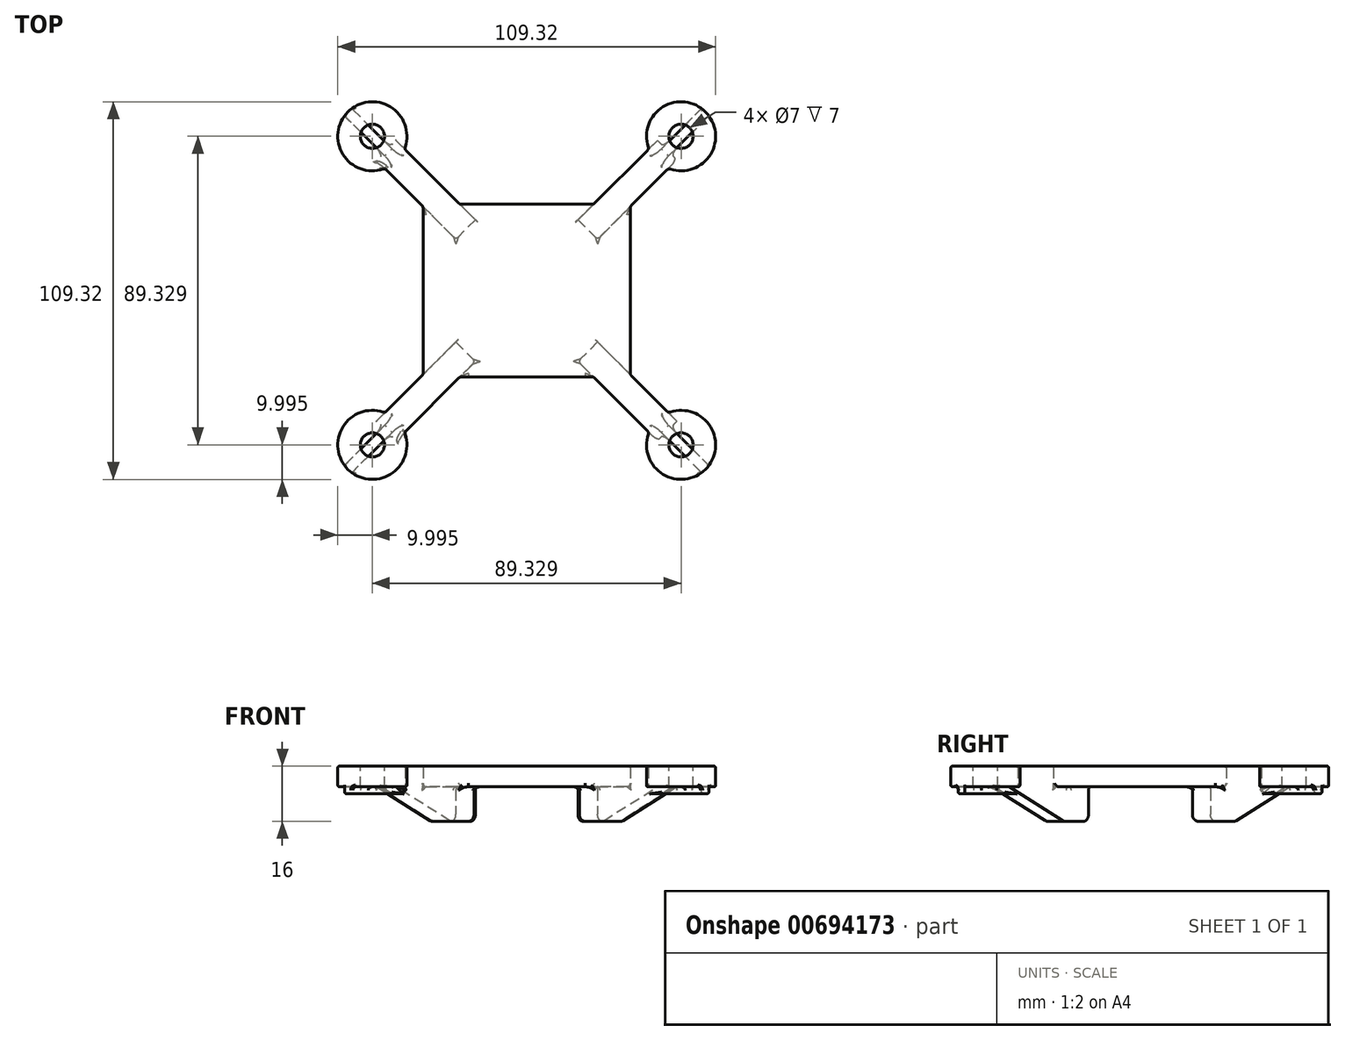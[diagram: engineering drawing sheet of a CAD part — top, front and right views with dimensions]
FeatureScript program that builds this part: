
annotation { "Feature Type Name" : "Feature", "Feature Type Description" : "" }
export const myFeature = defineFeature(function(context is Context, id is Id, definition is map)
    precondition{}
    {
        {
            var Q0;
            Q0=qCreatedBy(makeId("Top.planeOp"),FACE);
            var sketch = newSketch(context, id + "F0", { "sketchPlane" : qUnion([Q0])});
            skLineSegment(sketch, "E0.left", {"start": v(-30, 24.34) * mm, "end": v(-30, -24.34) * mm});
            skLineSegment(sketch, "E0.right", {"start": v(30, 24.34) * mm, "end": v(30, -24.34) * mm});
            skPoint(sketch, "E0.middle", {"position": v(0, 0) * mm});
            skLineSegment(sketch, "E1", {"start": v(-5.66, 0) * mm, "end": v(-30, 24.34) * mm, "construction": true});
            skLineSegment(sketch, "E2", {"start": v(-30, 24.34) * mm, "end": v(-41.01, 35.36) * mm});
            skLineSegment(sketch, "E3", {"start": v(0, 5.66) * mm, "end": v(-19.34, 25) * mm, "construction": true});
            skLineSegment(sketch, "E4", {"start": v(-19.34, 25) * mm, "end": v(-35.36, 41.01) * mm});
            skLineSegment(sketch, "E5", {"start": v(0, 5.66) * mm, "end": v(19.34, 25) * mm, "construction": true});
            skLineSegment(sketch, "E6", {"start": v(19.34, 25) * mm, "end": v(35.36, 41.01) * mm});
            skLineSegment(sketch, "E7", {"start": v(5.66, 0) * mm, "end": v(30, 24.34) * mm, "construction": true});
            skLineSegment(sketch, "E8", {"start": v(30, 24.34) * mm, "end": v(41.01, 35.36) * mm});
            skLineSegment(sketch, "E9", {"start": v(-5.66, 0) * mm, "end": v(-30, -24.34) * mm, "construction": true});
            skLineSegment(sketch, "E10", {"start": v(-30, -24.34) * mm, "end": v(-41.01, -35.36) * mm});
            skLineSegment(sketch, "E11", {"start": v(0, -5.66) * mm, "end": v(-19.34, -25) * mm, "construction": true});
            skLineSegment(sketch, "E12", {"start": v(-19.34, -25) * mm, "end": v(-35.36, -41.01) * mm});
            skLineSegment(sketch, "E13", {"start": v(0, -5.66) * mm, "end": v(19.34, -25) * mm, "construction": true});
            skLineSegment(sketch, "E14", {"start": v(19.34, -25) * mm, "end": v(35.36, -41.01) * mm});
            skLineSegment(sketch, "E15", {"start": v(5.66, 0) * mm, "end": v(30, -24.34) * mm, "construction": true});
            skLineSegment(sketch, "E16", {"start": v(30, -24.34) * mm, "end": v(41.01, -35.36) * mm});
            skLineSegment(sketch, "E17", {"start": v(0, 5.66) * mm, "end": v(0, -5.66) * mm, "construction": true});
            skLineSegment(sketch, "E18", {"start": v(-5.66, 0) * mm, "end": v(5.66, 0) * mm, "construction": true});
            skLineSegment(sketch, "E19", {"start": v(-19.34, 25) * mm, "end": v(19.34, 25) * mm});
            skLineSegment(sketch, "E20", {"start": v(-19.34, -25) * mm, "end": v(19.34, -25) * mm});
            skArc(sketch, "E21", {"start": v(-35.36, 41.01) * mm, "mid": v(-51.74, 51.74) * mm, "end": v(-41.01, 35.36) * mm});
            skArc(sketch, "E22", {"start": v(35.36, 41.01) * mm, "mid": v(51.74, 51.74) * mm, "end": v(41.01, 35.36) * mm});
            skArc(sketch, "E23", {"start": v(41.01, -35.36) * mm, "mid": v(51.74, -51.74) * mm, "end": v(35.36, -41.01) * mm});
            skArc(sketch, "E24", {"start": v(-41.01, -35.36) * mm, "mid": v(-51.74, -51.74) * mm, "end": v(-35.36, -41.01) * mm});
            skLineSegment(sketch, "E25", {"start": v(-35.36, -41.01) * mm, "end": v(-41.01, -35.36) * mm, "construction": true});
            skLineSegment(sketch, "E26", {"start": v(35.36, -41.01) * mm, "end": v(41.01, -35.36) * mm, "construction": true});
            skLineSegment(sketch, "E27", {"start": v(35.36, 41.01) * mm, "end": v(41.01, 35.36) * mm, "construction": true});
            skLineSegment(sketch, "E28", {"start": v(-35.36, 41.01) * mm, "end": v(-41.01, 35.36) * mm, "construction": true});
            skSolve(sketch);
        }
        {
            var Q0;
            Q0=qSketchRegion(id+"F0",true);
            extrude(context, id + "F1", {"entities" : qUnion([Q0]), "endBound" : BoundingType.SYMMETRIC, "depth" : 6 * mm, "offsetDistance" : 25.4 * mm});
        }
        {
            var Q0;
            Q0=makeQuery(id+"F1.opExtrude","SWEPT_FACE",FACE,{"disambiguationData":[OSD([sQuery(id+"F0.wireOp",EDGE,"E12")])]});
            cPlane(context, id + "F2", {"entities" : qUnion([Q0]), "cplaneType" : CPlaneType.OFFSET, "offset" : 0 * mm, "width" : 152.4 * mm, "height" : 152.4 * mm});
        }
        {
            var Q0;
            Q0=qCreatedBy(id+"F2.planeOp",FACE);
            var sketch = newSketch(context, id + "F3", { "sketchPlane" : qUnion([Q0])});
            skLineSegment(sketch, "E29", {"start": v(-57.5, -3) * mm, "end": v(-35, -13) * mm});
            skLineSegment(sketch, "E30", {"start": v(-35, -13) * mm, "end": v(-25, -13) * mm});
            skLineSegment(sketch, "E31", {"start": v(-25, -13) * mm, "end": v(-25, -3) * mm});
            skLineSegment(sketch, "E32", {"start": v(-25, -3) * mm, "end": v(-57.5, -3) * mm});
            skLineSegment(sketch, "E33", {"start": v(0, 36.74) * mm, "end": v(0, -57.68) * mm, "construction": true});
            skLineSegment(sketch, "E34.MirrorCS", {"start": v(25, -13) * mm, "end": v(25, -3) * mm});
            skLineSegment(sketch, "E35.MirrorCS", {"start": v(25, -3) * mm, "end": v(57.5, -3) * mm});
            skLineSegment(sketch, "E36.MirrorCS", {"start": v(57.5, -3) * mm, "end": v(35, -13) * mm});
            skLineSegment(sketch, "E37.MirrorCS", {"start": v(35, -13) * mm, "end": v(25, -13) * mm});
            skSolve(sketch);
        }
        {
            var Q0;
            Q0=qSketchRegion(id+"F3",true);
            var Q1;
            Q1=makeQuery(id+"F1.opExtrude","SWEPT_FACE",FACE,{"disambiguationData":[OSD([sQuery(id+"F0.wireOp",EDGE,"E10")])]});
            extrude(context, id + "F4", {"entities" : qUnion([Q0]), "operationType" : NewBodyOperationType.ADD, "endBound" : BoundingType.UP_TO_SURFACE, "oppositeDirection" : true, "depth" : 15 * mm, "endBoundEntityFace" : qUnion([Q1]), "offsetDistance" : 25.4 * mm});
        }
        {
            var Q0;
            Q0=makeQuery(id+"F1.opExtrude","SWEPT_FACE",FACE,{"disambiguationData":[OSD([sQuery(id+"F0.wireOp",EDGE,"E2")])]});
            cPlane(context, id + "F5", {"entities" : qUnion([Q0]), "cplaneType" : CPlaneType.OFFSET, "offset" : 0 * mm, "width" : 152.4 * mm, "height" : 152.4 * mm});
        }
        {
            var Q0;
            Q0=qCreatedBy(id+"F5.planeOp",FACE);
            var sketch = newSketch(context, id + "F6", { "sketchPlane" : qUnion([Q0])});
            skLineSegment(sketch, "E38", {"start": v(0, 30.92) * mm, "end": v(0, -51.6) * mm, "construction": true});
            skLineSegment(sketch, "E39", {"start": v(-25, -3) * mm, "end": v(-57.5, -3) * mm});
            skLineSegment(sketch, "E40", {"start": v(-57.5, -3) * mm, "end": v(-35, -13) * mm});
            skLineSegment(sketch, "E41", {"start": v(-35, -13) * mm, "end": v(-25, -13) * mm});
            skLineSegment(sketch, "E42", {"start": v(-25, -13) * mm, "end": v(-25, -3) * mm});
            skLineSegment(sketch, "E43.MirrorCS", {"start": v(25, -13) * mm, "end": v(25, -3) * mm});
            skLineSegment(sketch, "E44.MirrorCS", {"start": v(25, -3) * mm, "end": v(57.5, -3) * mm});
            skLineSegment(sketch, "E45.MirrorCS", {"start": v(57.5, -3) * mm, "end": v(35, -13) * mm});
            skLineSegment(sketch, "E46.MirrorCS", {"start": v(35, -13) * mm, "end": v(25, -13) * mm});
            skSolve(sketch);
        }
        {
            var Q0;
            Q0=qSketchRegion(id+"F6",true);
            var Q1;
            Q1=makeQuery(id+"F1.opExtrude","SWEPT_FACE",FACE,{"disambiguationData":[OSD([sQuery(id+"F0.wireOp",EDGE,"E4")])]});
            extrude(context, id + "F7", {"entities" : qUnion([Q0]), "operationType" : NewBodyOperationType.ADD, "endBound" : BoundingType.UP_TO_SURFACE, "oppositeDirection" : true, "depth" : 25.4 * mm, "endBoundEntityFace" : qUnion([Q1]), "offsetDistance" : 25.4 * mm});
        }
        {
            var Q0;
            Q0=makeQuery(id+"F1.opExtrude","CAP_FACE",FACE,{"disambiguationData":[OSD([sQuery(id+"F0.wireOp",EDGE,"E0.left"),sQuery(id+"F0.wireOp",EDGE,"E0.right"),sQuery(id+"F0.wireOp",EDGE,"E2"),sQuery(id+"F0.wireOp",EDGE,"E4"),sQuery(id+"F0.wireOp",EDGE,"E6"),sQuery(id+"F0.wireOp",EDGE,"E8"),sQuery(id+"F0.wireOp",EDGE,"E10"),sQuery(id+"F0.wireOp",EDGE,"E12"),sQuery(id+"F0.wireOp",EDGE,"E14"),sQuery(id+"F0.wireOp",EDGE,"E16"),sQuery(id+"F0.wireOp",EDGE,"U0aqChP4-xO90-fPp5-lgJY-XNEjWLDpO9Pw"),sQuery(id+"F0.wireOp",EDGE,"E19"),sQuery(id+"F0.wireOp",EDGE,"cbbJuHwt-aKsD-GqAp-nsX4-LxCeeRADLvEd"),sQuery(id+"F0.wireOp",EDGE,"bN4DHRRX-U12u-KNd2-8Xf1-whkmB7apZKRc"),sQuery(id+"F0.wireOp",EDGE,"E20"),sQuery(id+"F0.wireOp",EDGE,"p7OAdbqt-RvIZ-X6Lu-gwcG-EmbuIjXrlg1e"),sQuery(id+"F0.wireOp",EDGE,"E21"),sQuery(id+"F0.wireOp",EDGE,"E22"),sQuery(id+"F0.wireOp",EDGE,"E23"),sQuery(id+"F0.wireOp",EDGE,"E24")])],"isStart":false});
            var sketch = newSketch(context, id + "F8", { "sketchPlane" : qUnion([Q0])});
            skCircle(sketch, "E47", {"center": v(-44.66, 44.66) * mm, "radius": 3.5 * mm});
            skCircle(sketch, "E48", {"center": v(44.66, 44.66) * mm, "radius": 3.5 * mm});
            skCircle(sketch, "E49", {"center": v(44.66, -44.66) * mm, "radius": 3.5 * mm});
            skCircle(sketch, "E50", {"center": v(-44.66, -44.66) * mm, "radius": 3.5 * mm});
            skSolve(sketch);
        }
        {
            var Q0;
            Q0=qSketchRegion(id+"F8",true);
            extrude(context, id + "F9", {"entities" : qUnion([Q0]), "operationType" : NewBodyOperationType.REMOVE, "endBound" : BoundingType.THROUGH_ALL, "oppositeDirection" : true, "depth" : 25.4 * mm, "offsetDistance" : 25.4 * mm});
        }
        {
            var Q0;
            {var subQ0=sQuery(id+"F0.wireOp",EDGE,"E24");var subQ2=sQuery(id+"F0.wireOp",EDGE,"E12");var subQ3=sQuery(id+"F0.wireOp",EDGE,"E10");Q0=makeQuery(id+"F4.boolean.opBoolean","SPLIT",FACE,{"disambiguationData":[TD([makeQuery(id+"F1.opExtrude","SWEPT_FACE",FACE,{"disambiguationData":[OSD([subQ0])]})])],"derivedFrom":makeQuery(id+"F1.opExtrude","CAP_FACE",FACE,{"disambiguationData":[OSD([sQuery(id+"F0.wireOp",EDGE,"E0.left"),sQuery(id+"F0.wireOp",EDGE,"E0.right"),sQuery(id+"F0.wireOp",EDGE,"E2"),sQuery(id+"F0.wireOp",EDGE,"E4"),sQuery(id+"F0.wireOp",EDGE,"E6"),sQuery(id+"F0.wireOp",EDGE,"E8"),subQ3,subQ2,sQuery(id+"F0.wireOp",EDGE,"E14"),sQuery(id+"F0.wireOp",EDGE,"E16"),sQuery(id+"F0.wireOp",EDGE,"E19"),sQuery(id+"F0.wireOp",EDGE,"E20"),sQuery(id+"F0.wireOp",EDGE,"E21"),sQuery(id+"F0.wireOp",EDGE,"E22"),sQuery(id+"F0.wireOp",EDGE,"E23"),subQ0])],"isStart":true})});}
            var sketch = newSketch(context, id + "F10", { "sketchPlane" : qUnion([Q0])});
            skLineSegment(sketch, "E51", {"start": v(-52.72, 50.6) * mm, "end": v(-34.77, 32.64) * mm});
            skLineSegment(sketch, "E52", {"start": v(-34.77, 32.64) * mm, "end": v(-32.64, 34.77) * mm});
            skLineSegment(sketch, "E53", {"start": v(-32.64, 34.77) * mm, "end": v(-50.6, 52.72) * mm});
            skLineSegment(sketch, "E54", {"start": v(-54.84, 54.84) * mm, "end": v(59.9, -59.9) * mm, "construction": true});
            skLineSegment(sketch, "E55", {"start": v(57.6, 57.6) * mm, "end": v(-59.22, -59.22) * mm, "construction": true});
            skArc(sketch, "E56", {"start": v(-50.6, 52.72) * mm, "mid": v(-51.74, 51.74) * mm, "end": v(-52.72, 50.6) * mm});
            skLineSegment(sketch, "E57.1.0", {"start": v(-34.77, -32.64) * mm, "end": v(-52.72, -50.6) * mm});
            skArc(sketch, "E57.1.1", {"start": v(-52.72, -50.6) * mm, "mid": v(-51.74, -51.74) * mm, "end": v(-50.6, -52.72) * mm});
            skLineSegment(sketch, "E57.1.2", {"start": v(-50.6, -52.72) * mm, "end": v(-32.64, -34.77) * mm});
            skLineSegment(sketch, "E57.1.3", {"start": v(-32.64, -34.77) * mm, "end": v(-34.77, -32.64) * mm});
            skLineSegment(sketch, "E57.2.0", {"start": v(32.64, -34.77) * mm, "end": v(50.6, -52.72) * mm});
            skArc(sketch, "E57.2.1", {"start": v(50.6, -52.72) * mm, "mid": v(51.74, -51.74) * mm, "end": v(52.72, -50.6) * mm});
            skLineSegment(sketch, "E57.2.2", {"start": v(52.72, -50.6) * mm, "end": v(34.77, -32.64) * mm});
            skLineSegment(sketch, "E57.2.3", {"start": v(34.77, -32.64) * mm, "end": v(32.64, -34.77) * mm});
            skLineSegment(sketch, "E57.3.0", {"start": v(34.77, 32.64) * mm, "end": v(52.72, 50.6) * mm});
            skArc(sketch, "E57.3.1", {"start": v(52.72, 50.6) * mm, "mid": v(51.74, 51.74) * mm, "end": v(50.6, 52.72) * mm});
            skLineSegment(sketch, "E57.3.2", {"start": v(50.6, 52.72) * mm, "end": v(32.64, 34.77) * mm});
            skLineSegment(sketch, "E57.3.3", {"start": v(32.64, 34.77) * mm, "end": v(34.77, 32.64) * mm});
            skPoint(sketch, "E57.center", {"position": v(0, 0) * mm});
            skSolve(sketch);
        }
        {
            var Q0;
            Q0 = qSketchRegion(id + "F10", true);
            extrude(context, id + "F11", {"entities" : qUnion([Q0]), "operationType" : NewBodyOperationType.ADD, "depth" : 2 * mm, "offsetDistance" : 25 * mm});
        }
        {
            var Q0;
            {var subQ0=sQuery(id+"F3.wireOp",EDGE,"E32");var subQ2=sQuery(id+"F0.wireOp",EDGE,"E20");Q0=makeQuery(id+"F4.boolean.opBoolean","SPLIT",EDGE,{"disambiguationData":[TD([makeQuery(id+"F1.opExtrude","SWEPT_FACE",FACE,{"disambiguationData":[OSD([subQ2])]})])],"derivedFrom":makeQuery(id+"F4.opExtrude","CAP_EDGE",EDGE,{"disambiguationData":[OSD([subQ0])],"isStart":true})});}
            var Q1;
            Q1=makeQuery(id+"F4.opExtrude","SWEPT_EDGE",EDGE,{"disambiguationData":[OSD([sQuery(id+"F3.wireOp",EDGE,"E31"),sQuery(id+"F3.wireOp",EDGE,"E32")])]});
            var Q2;
            {var subQ0=sQuery(id+"F0.wireOp",EDGE,"E10");var subQ1=makeQuery(id+"F1.opExtrude","SWEPT_FACE",FACE,{"disambiguationData":[OSD([subQ0])]});var subQ2=sQuery(id+"F0.wireOp",EDGE,"E0.left");Q2=makeQuery(id+"F4.boolean.opBoolean","SPLIT",EDGE,{"disambiguationData":[TD([makeQuery(id+"F1.opExtrude","SWEPT_FACE",FACE,{"disambiguationData":[OSD([subQ2])]})])],"derivedFrom":makeQuery(id+"F4.opExtrude","TWEAK_EDGE",EDGE,{"derivedFrom":[subQ1,makeQuery(id+"F3.imprint","IMPRINT",EDGE,{"derivedFrom":sQuery(id+"F3.wireOp",EDGE,"E32")})]})});}
            var Q3;
            Q3=makeQuery(id+"F7.opExtrude","SWEPT_EDGE",EDGE,{"disambiguationData":[OSD([sQuery(id+"F6.wireOp",EDGE,"E43.MirrorCS"),sQuery(id+"F6.wireOp",EDGE,"E44.MirrorCS")])]});
            var Q4;
            {var subQ0=sQuery(id+"F0.wireOp",EDGE,"E0.right");var subQ1=sQuery(id+"F0.wireOp",EDGE,"E4");Q4=makeQuery(id+"F7.boolean.opBoolean","SPLIT",EDGE,{"disambiguationData":[TD([makeQuery(id+"F1.opExtrude","SWEPT_FACE",FACE,{"disambiguationData":[OSD([subQ0])]})])],"derivedFrom":makeQuery(id+"F7.opExtrude","TWEAK_EDGE",EDGE,{"derivedFrom":[makeQuery(id+"F1.opExtrude","SWEPT_FACE",FACE,{"disambiguationData":[OSD([subQ1])]}),makeQuery(id+"F6.imprint","IMPRINT",EDGE,{"derivedFrom":sQuery(id+"F6.wireOp",EDGE,"E44.MirrorCS")})]})});}
            var Q5;
            {var subQ1=sQuery(id+"F0.wireOp",EDGE,"E20");var subQ3=sQuery(id+"F6.wireOp",EDGE,"E44.MirrorCS");Q5=makeQuery(id+"F7.boolean.opBoolean","SPLIT",EDGE,{"disambiguationData":[TD([makeQuery(id+"F1.opExtrude","SWEPT_FACE",FACE,{"disambiguationData":[OSD([subQ1])]})])],"derivedFrom":makeQuery(id+"F7.opExtrude","CAP_EDGE",EDGE,{"disambiguationData":[OSD([subQ3])],"isStart":true})});}
            var Q6;
            Q6=makeQuery(id+"F1.opExtrude","SWEPT_EDGE",EDGE,{"disambiguationData":[OSD([sQuery(id+"F0.wireOp",EDGE,"E14"),sQuery(id+"F0.wireOp",EDGE,"E20")])]});
            var Q7;
            Q7=makeQuery(id+"F1.opExtrude","SWEPT_EDGE",EDGE,{"disambiguationData":[OSD([sQuery(id+"F0.wireOp",EDGE,"E12"),sQuery(id+"F0.wireOp",EDGE,"E20")])]});
            var Q8;
            Q8=makeQuery(id+"F1.opExtrude","SWEPT_EDGE",EDGE,{"disambiguationData":[OSD([sQuery(id+"F0.wireOp",EDGE,"E0.left"),sQuery(id+"F0.wireOp",EDGE,"E10")])]});
            var Q9;
            Q9=makeQuery(id+"F1.opExtrude","SWEPT_EDGE",EDGE,{"disambiguationData":[OSD([sQuery(id+"F0.wireOp",EDGE,"E0.left"),sQuery(id+"F0.wireOp",EDGE,"E2")])]});
            var Q10;
            {var subQ2=sQuery(id+"F6.wireOp",EDGE,"E39");var subQ3=sQuery(id+"F0.wireOp",EDGE,"E0.left");Q10=makeQuery(id+"F7.boolean.opBoolean","SPLIT",EDGE,{"disambiguationData":[TD([makeQuery(id+"F1.opExtrude","SWEPT_FACE",FACE,{"disambiguationData":[OSD([subQ3])]})])],"derivedFrom":makeQuery(id+"F7.opExtrude","CAP_EDGE",EDGE,{"disambiguationData":[OSD([subQ2])],"isStart":true})});}
            var Q11;
            Q11=makeQuery(id+"F7.opExtrude","SWEPT_EDGE",EDGE,{"disambiguationData":[OSD([sQuery(id+"F6.wireOp",EDGE,"E39"),sQuery(id+"F6.wireOp",EDGE,"E42")])]});
            var Q12;
            {var subQ0=sQuery(id+"F0.wireOp",EDGE,"E19");var subQ1=sQuery(id+"F0.wireOp",EDGE,"E4");var subQ2=makeQuery(id+"F1.opExtrude","SWEPT_FACE",FACE,{"disambiguationData":[OSD([subQ1])]});Q12=makeQuery(id+"F7.boolean.opBoolean","SPLIT",EDGE,{"disambiguationData":[TD([makeQuery(id+"F1.opExtrude","SWEPT_FACE",FACE,{"disambiguationData":[OSD([subQ0])]})])],"derivedFrom":makeQuery(id+"F7.opExtrude","TWEAK_EDGE",EDGE,{"derivedFrom":[subQ2,makeQuery(id+"F6.imprint","IMPRINT",EDGE,{"derivedFrom":sQuery(id+"F6.wireOp",EDGE,"E39")})]})});}
            var Q13;
            Q13=makeQuery(id+"F1.opExtrude","SWEPT_EDGE",EDGE,{"disambiguationData":[OSD([sQuery(id+"F0.wireOp",EDGE,"E4"),sQuery(id+"F0.wireOp",EDGE,"E19")])]});
            var Q14;
            Q14=makeQuery(id+"F4.opExtrude","SWEPT_EDGE",EDGE,{"disambiguationData":[OSD([sQuery(id+"F3.wireOp",EDGE,"E34.MirrorCS"),sQuery(id+"F3.wireOp",EDGE,"E35.MirrorCS")])]});
            var Q15;
            {var subQ0=sQuery(id+"F0.wireOp",EDGE,"E19");var subQ1=sQuery(id+"F0.wireOp",EDGE,"E10");Q15=makeQuery(id+"F4.boolean.opBoolean","SPLIT",EDGE,{"disambiguationData":[TD([makeQuery(id+"F1.opExtrude","SWEPT_FACE",FACE,{"disambiguationData":[OSD([subQ0])]})])],"derivedFrom":makeQuery(id+"F4.opExtrude","TWEAK_EDGE",EDGE,{"derivedFrom":[makeQuery(id+"F1.opExtrude","SWEPT_FACE",FACE,{"disambiguationData":[OSD([subQ1])]}),makeQuery(id+"F3.imprint","IMPRINT",EDGE,{"derivedFrom":sQuery(id+"F3.wireOp",EDGE,"E35.MirrorCS")})]})});}
            var Q16;
            Q16=makeQuery(id+"F1.opExtrude","SWEPT_EDGE",EDGE,{"disambiguationData":[OSD([sQuery(id+"F0.wireOp",EDGE,"E6"),sQuery(id+"F0.wireOp",EDGE,"E19")])]});
            var Q17;
            {var subQ2=sQuery(id+"F0.wireOp",EDGE,"E0.right");var subQ3=sQuery(id+"F3.wireOp",EDGE,"E35.MirrorCS");Q17=makeQuery(id+"F4.boolean.opBoolean","SPLIT",EDGE,{"disambiguationData":[TD([makeQuery(id+"F1.opExtrude","SWEPT_FACE",FACE,{"disambiguationData":[OSD([subQ2])]})])],"derivedFrom":makeQuery(id+"F4.opExtrude","CAP_EDGE",EDGE,{"disambiguationData":[OSD([subQ3])],"isStart":true})});}
            var Q18;
            Q18=makeQuery(id+"F1.opExtrude","SWEPT_EDGE",EDGE,{"disambiguationData":[OSD([sQuery(id+"F0.wireOp",EDGE,"E6"),sQuery(id+"F0.wireOp",EDGE,"E22")])]});
            var Q19;
            Q19=makeQuery(id+"F1.opExtrude","SWEPT_EDGE",EDGE,{"disambiguationData":[OSD([sQuery(id+"F0.wireOp",EDGE,"E0.right"),sQuery(id+"F0.wireOp",EDGE,"E8")])]});
            var Q20;
            Q20=makeQuery(id+"F1.opExtrude","SWEPT_EDGE",EDGE,{"disambiguationData":[OSD([sQuery(id+"F0.wireOp",EDGE,"E0.right"),sQuery(id+"F0.wireOp",EDGE,"E16")])]});
            var Q21;
            {var subQ0=sQuery(id+"F0.wireOp",EDGE,"E22");var subQ2=sQuery(id+"F0.wireOp",EDGE,"E10");Q21=makeQuery(id+"F4.boolean.opBoolean","SPLIT",EDGE,{"disambiguationData":[TD([makeQuery(id+"F1.opExtrude","SWEPT_FACE",FACE,{"disambiguationData":[OSD([subQ0])]})])],"derivedFrom":makeQuery(id+"F4.opExtrude","TWEAK_EDGE",EDGE,{"derivedFrom":[makeQuery(id+"F1.opExtrude","SWEPT_FACE",FACE,{"disambiguationData":[OSD([subQ2])]}),makeQuery(id+"F3.imprint","IMPRINT",EDGE,{"derivedFrom":sQuery(id+"F3.wireOp",EDGE,"E35.MirrorCS")})]})});}
            var Q22;
            {var subQ1=sQuery(id+"F3.wireOp",EDGE,"E36.MirrorCS");var subQ2=sQuery(id+"F0.wireOp",EDGE,"E6");Q22=makeQuery(id+"F11.boolean.opBoolean","SPLIT",EDGE,{"disambiguationData":[TD([makeQuery(id+"F1.opExtrude","SWEPT_FACE",FACE,{"disambiguationData":[OSD([subQ2])]})])],"derivedFrom":makeQuery(id+"F4.opExtrude","SWEPT_EDGE",EDGE,{"disambiguationData":[OSD([sQuery(id+"F3.wireOp",EDGE,"E35.MirrorCS"),subQ1])]})});}
            var Q23;
            Q23=makeQuery(id+"F11.boolean.opBoolean","INTERSECT",EDGE,{"derivedFrom":[makeQuery(id+"F4.opExtrude","SWEPT_FACE",FACE,{"disambiguationData":[OSD([sQuery(id+"F3.wireOp",EDGE,"E36.MirrorCS")])]}),makeQuery(id+"F11.opExtrude","SWEPT_FACE",FACE,{"disambiguationData":[OSD([sQuery(id+"F10.wireOp",EDGE,"E57.2.0")])]})]});
            var Q24;
            Q24=makeQuery(id+"F11.boolean.opBoolean","INTERSECT",EDGE,{"derivedFrom":[makeQuery(id+"F4.opExtrude","SWEPT_FACE",FACE,{"disambiguationData":[OSD([sQuery(id+"F3.wireOp",EDGE,"E36.MirrorCS")])]}),makeQuery(id+"F11.opExtrude","CAP_FACE",FACE,{"disambiguationData":[OSD([sQuery(id+"F10.wireOp",EDGE,"E57.2.0"),sQuery(id+"F10.wireOp",EDGE,"E57.2.1"),sQuery(id+"F10.wireOp",EDGE,"E57.2.2"),sQuery(id+"F10.wireOp",EDGE,"E57.2.3")])],"isStart":false})]});
            var Q25;
            Q25=makeQuery(id+"F11.boolean.opBoolean","INTERSECT",EDGE,{"derivedFrom":[makeQuery(id+"F4.opExtrude","SWEPT_FACE",FACE,{"disambiguationData":[OSD([sQuery(id+"F3.wireOp",EDGE,"E36.MirrorCS")])]}),makeQuery(id+"F11.opExtrude","SWEPT_FACE",FACE,{"disambiguationData":[OSD([sQuery(id+"F10.wireOp",EDGE,"E57.2.2")])]})]});
            var Q26;
            {var subQ0=sQuery(id+"F3.wireOp",EDGE,"E36.MirrorCS");var subQ1=sQuery(id+"F3.wireOp",EDGE,"E35.MirrorCS");var subQ2=sQuery(id+"F0.wireOp",EDGE,"E8");Q26=makeQuery(id+"F11.boolean.opBoolean","SPLIT",EDGE,{"disambiguationData":[TD([makeQuery(id+"F1.opExtrude","SWEPT_FACE",FACE,{"disambiguationData":[OSD([subQ2])]})])],"derivedFrom":makeQuery(id+"F4.opExtrude","SWEPT_EDGE",EDGE,{"disambiguationData":[OSD([subQ1,subQ0])]})});}
            var Q27;
            {var subQ1=sQuery(id+"F3.wireOp",EDGE,"E35.MirrorCS");var subQ2=sQuery(id+"F0.wireOp",EDGE,"E22");Q27=makeQuery(id+"F4.boolean.opBoolean","SPLIT",EDGE,{"disambiguationData":[TD([makeQuery(id+"F1.opExtrude","SWEPT_FACE",FACE,{"disambiguationData":[OSD([subQ2])]})])],"derivedFrom":makeQuery(id+"F4.opExtrude","CAP_EDGE",EDGE,{"disambiguationData":[OSD([subQ1])],"isStart":true})});}
            var Q28;
            Q28=makeQuery(id+"F1.opExtrude","SWEPT_EDGE",EDGE,{"disambiguationData":[OSD([sQuery(id+"F0.wireOp",EDGE,"E8"),sQuery(id+"F0.wireOp",EDGE,"E22")])]});
            var Q29;
            {var subQ0=sQuery(id+"F10.wireOp",EDGE,"E57.2.2");var subQ2=sQuery(id+"F0.wireOp",EDGE,"E22");var subQ3=makeQuery(id+"F1.opExtrude","CAP_FACE",FACE,{"disambiguationData":[OSD([sQuery(id+"F0.wireOp",EDGE,"E0.left"),sQuery(id+"F0.wireOp",EDGE,"E0.right"),sQuery(id+"F0.wireOp",EDGE,"E2"),sQuery(id+"F0.wireOp",EDGE,"E4"),sQuery(id+"F0.wireOp",EDGE,"E6"),sQuery(id+"F0.wireOp",EDGE,"E8"),sQuery(id+"F0.wireOp",EDGE,"E10"),sQuery(id+"F0.wireOp",EDGE,"E12"),sQuery(id+"F0.wireOp",EDGE,"E14"),sQuery(id+"F0.wireOp",EDGE,"E16"),sQuery(id+"F0.wireOp",EDGE,"E19"),sQuery(id+"F0.wireOp",EDGE,"E20"),sQuery(id+"F0.wireOp",EDGE,"E21"),subQ2,sQuery(id+"F0.wireOp",EDGE,"E23"),sQuery(id+"F0.wireOp",EDGE,"E24")])],"isStart":true});var subQ4=makeQuery(id+"F11.opExtrude","SWEPT_FACE",FACE,{"disambiguationData":[OSD([subQ0])]});Q29=makeQuery(id+"F11.boolean.opBoolean","SPLIT",EDGE,{"disambiguationData":[topologyDisambiguationEdgeConnected([subQ3,subQ4]),TD([makeQuery(id+"F1.opExtrude","SWEPT_FACE",FACE,{"disambiguationData":[OSD([subQ2])]})])],"derivedFrom":makeQuery(id+"F11.opExtrude","CAP_EDGE",EDGE,{"disambiguationData":[OSD([subQ0])],"isStart":true})});}
            var Q30;
            {var subQ0=sQuery(id+"F10.wireOp",EDGE,"E57.2.0");var subQ1=makeQuery(id+"F11.opExtrude","SWEPT_FACE",FACE,{"disambiguationData":[OSD([subQ0])]});var subQ2=sQuery(id+"F0.wireOp",EDGE,"E22");var subQ4=makeQuery(id+"F1.opExtrude","CAP_FACE",FACE,{"disambiguationData":[OSD([sQuery(id+"F0.wireOp",EDGE,"E0.left"),sQuery(id+"F0.wireOp",EDGE,"E0.right"),sQuery(id+"F0.wireOp",EDGE,"E2"),sQuery(id+"F0.wireOp",EDGE,"E4"),sQuery(id+"F0.wireOp",EDGE,"E6"),sQuery(id+"F0.wireOp",EDGE,"E8"),sQuery(id+"F0.wireOp",EDGE,"E10"),sQuery(id+"F0.wireOp",EDGE,"E12"),sQuery(id+"F0.wireOp",EDGE,"E14"),sQuery(id+"F0.wireOp",EDGE,"E16"),sQuery(id+"F0.wireOp",EDGE,"E19"),sQuery(id+"F0.wireOp",EDGE,"E20"),sQuery(id+"F0.wireOp",EDGE,"E21"),subQ2,sQuery(id+"F0.wireOp",EDGE,"E23"),sQuery(id+"F0.wireOp",EDGE,"E24")])],"isStart":true});Q30=makeQuery(id+"F11.boolean.opBoolean","SPLIT",EDGE,{"disambiguationData":[topologyDisambiguationEdgeConnected([subQ4,subQ1]),TD([makeQuery(id+"F1.opExtrude","SWEPT_FACE",FACE,{"disambiguationData":[OSD([subQ2])]})])],"derivedFrom":makeQuery(id+"F11.opExtrude","CAP_EDGE",EDGE,{"disambiguationData":[OSD([subQ0])],"isStart":true})});}
            var Q31;
            Q31=makeQuery(id+"F1.opExtrude","SWEPT_EDGE",EDGE,{"disambiguationData":[OSD([sQuery(id+"F0.wireOp",EDGE,"E2"),sQuery(id+"F0.wireOp",EDGE,"E21")])]});
            var Q32;
            {var subQ1=sQuery(id+"F6.wireOp",EDGE,"E39");var subQ3=sQuery(id+"F0.wireOp",EDGE,"E21");Q32=makeQuery(id+"F7.boolean.opBoolean","SPLIT",EDGE,{"disambiguationData":[TD([makeQuery(id+"F1.opExtrude","SWEPT_FACE",FACE,{"disambiguationData":[OSD([subQ3])]})])],"derivedFrom":makeQuery(id+"F7.opExtrude","CAP_EDGE",EDGE,{"disambiguationData":[OSD([subQ1])],"isStart":true})});}
            var Q33;
            {var subQ0=sQuery(id+"F6.wireOp",EDGE,"E40");var subQ1=sQuery(id+"F6.wireOp",EDGE,"E39");var subQ2=sQuery(id+"F0.wireOp",EDGE,"E2");Q33=makeQuery(id+"F11.boolean.opBoolean","SPLIT",EDGE,{"disambiguationData":[TD([makeQuery(id+"F1.opExtrude","SWEPT_FACE",FACE,{"disambiguationData":[OSD([subQ2])]})])],"derivedFrom":makeQuery(id+"F7.opExtrude","SWEPT_EDGE",EDGE,{"disambiguationData":[OSD([subQ1,subQ0])]})});}
            var Q34;
            Q34=makeQuery(id+"F11.boolean.opBoolean","INTERSECT",EDGE,{"derivedFrom":[makeQuery(id+"F7.opExtrude","SWEPT_FACE",FACE,{"disambiguationData":[OSD([sQuery(id+"F6.wireOp",EDGE,"E40")])]}),makeQuery(id+"F11.opExtrude","SWEPT_FACE",FACE,{"disambiguationData":[OSD([sQuery(id+"F10.wireOp",EDGE,"E57.1.0")])]})]});
            var Q35;
            Q35=makeQuery(id+"F11.boolean.opBoolean","INTERSECT",EDGE,{"derivedFrom":[makeQuery(id+"F7.opExtrude","SWEPT_FACE",FACE,{"disambiguationData":[OSD([sQuery(id+"F6.wireOp",EDGE,"E40")])]}),makeQuery(id+"F11.opExtrude","CAP_FACE",FACE,{"disambiguationData":[OSD([sQuery(id+"F10.wireOp",EDGE,"E57.1.0"),sQuery(id+"F10.wireOp",EDGE,"E57.1.1"),sQuery(id+"F10.wireOp",EDGE,"E57.1.2"),sQuery(id+"F10.wireOp",EDGE,"E57.1.3")])],"isStart":false})]});
            var Q36;
            Q36=makeQuery(id+"F11.boolean.opBoolean","INTERSECT",EDGE,{"derivedFrom":[makeQuery(id+"F7.opExtrude","SWEPT_FACE",FACE,{"disambiguationData":[OSD([sQuery(id+"F6.wireOp",EDGE,"E40")])]}),makeQuery(id+"F11.opExtrude","SWEPT_FACE",FACE,{"disambiguationData":[OSD([sQuery(id+"F10.wireOp",EDGE,"E57.1.2")])]})]});
            var Q37;
            {var subQ0=sQuery(id+"F0.wireOp",EDGE,"E4");var subQ1=sQuery(id+"F6.wireOp",EDGE,"E40");Q37=makeQuery(id+"F11.boolean.opBoolean","SPLIT",EDGE,{"disambiguationData":[TD([makeQuery(id+"F1.opExtrude","SWEPT_FACE",FACE,{"disambiguationData":[OSD([subQ0])]})])],"derivedFrom":makeQuery(id+"F7.opExtrude","SWEPT_EDGE",EDGE,{"disambiguationData":[OSD([sQuery(id+"F6.wireOp",EDGE,"E39"),subQ1])]})});}
            var Q38;
            {var subQ0=sQuery(id+"F0.wireOp",EDGE,"E21");var subQ1=sQuery(id+"F0.wireOp",EDGE,"E4");var subQ2=makeQuery(id+"F1.opExtrude","SWEPT_FACE",FACE,{"disambiguationData":[OSD([subQ1])]});Q38=makeQuery(id+"F7.boolean.opBoolean","SPLIT",EDGE,{"disambiguationData":[TD([makeQuery(id+"F1.opExtrude","SWEPT_FACE",FACE,{"disambiguationData":[OSD([subQ0])]})])],"derivedFrom":makeQuery(id+"F7.opExtrude","TWEAK_EDGE",EDGE,{"derivedFrom":[subQ2,makeQuery(id+"F6.imprint","IMPRINT",EDGE,{"derivedFrom":sQuery(id+"F6.wireOp",EDGE,"E39")})]})});}
            var Q39;
            Q39=makeQuery(id+"F1.opExtrude","SWEPT_EDGE",EDGE,{"disambiguationData":[OSD([sQuery(id+"F0.wireOp",EDGE,"E4"),sQuery(id+"F0.wireOp",EDGE,"E21")])]});
            var Q40;
            {var subQ0=sQuery(id+"F10.wireOp",EDGE,"E57.1.2");var subQ2=sQuery(id+"F0.wireOp",EDGE,"E21");var subQ3=makeQuery(id+"F1.opExtrude","CAP_FACE",FACE,{"disambiguationData":[OSD([sQuery(id+"F0.wireOp",EDGE,"E0.left"),sQuery(id+"F0.wireOp",EDGE,"E0.right"),sQuery(id+"F0.wireOp",EDGE,"E2"),sQuery(id+"F0.wireOp",EDGE,"E4"),sQuery(id+"F0.wireOp",EDGE,"E6"),sQuery(id+"F0.wireOp",EDGE,"E8"),sQuery(id+"F0.wireOp",EDGE,"E10"),sQuery(id+"F0.wireOp",EDGE,"E12"),sQuery(id+"F0.wireOp",EDGE,"E14"),sQuery(id+"F0.wireOp",EDGE,"E16"),sQuery(id+"F0.wireOp",EDGE,"E19"),sQuery(id+"F0.wireOp",EDGE,"E20"),subQ2,sQuery(id+"F0.wireOp",EDGE,"E22"),sQuery(id+"F0.wireOp",EDGE,"E23"),sQuery(id+"F0.wireOp",EDGE,"E24")])],"isStart":true});var subQ4=makeQuery(id+"F11.opExtrude","SWEPT_FACE",FACE,{"disambiguationData":[OSD([subQ0])]});Q40=makeQuery(id+"F11.boolean.opBoolean","SPLIT",EDGE,{"disambiguationData":[topologyDisambiguationEdgeConnected([subQ3,subQ4]),TD([makeQuery(id+"F1.opExtrude","SWEPT_FACE",FACE,{"disambiguationData":[OSD([subQ2])]})])],"derivedFrom":makeQuery(id+"F11.opExtrude","CAP_EDGE",EDGE,{"disambiguationData":[OSD([subQ0])],"isStart":true})});}
            var Q41;
            {var subQ0=sQuery(id+"F10.wireOp",EDGE,"E57.1.0");var subQ1=makeQuery(id+"F11.opExtrude","SWEPT_FACE",FACE,{"disambiguationData":[OSD([subQ0])]});var subQ2=sQuery(id+"F0.wireOp",EDGE,"E21");var subQ3=makeQuery(id+"F1.opExtrude","CAP_FACE",FACE,{"disambiguationData":[OSD([sQuery(id+"F0.wireOp",EDGE,"E0.left"),sQuery(id+"F0.wireOp",EDGE,"E0.right"),sQuery(id+"F0.wireOp",EDGE,"E2"),sQuery(id+"F0.wireOp",EDGE,"E4"),sQuery(id+"F0.wireOp",EDGE,"E6"),sQuery(id+"F0.wireOp",EDGE,"E8"),sQuery(id+"F0.wireOp",EDGE,"E10"),sQuery(id+"F0.wireOp",EDGE,"E12"),sQuery(id+"F0.wireOp",EDGE,"E14"),sQuery(id+"F0.wireOp",EDGE,"E16"),sQuery(id+"F0.wireOp",EDGE,"E19"),sQuery(id+"F0.wireOp",EDGE,"E20"),subQ2,sQuery(id+"F0.wireOp",EDGE,"E22"),sQuery(id+"F0.wireOp",EDGE,"E23"),sQuery(id+"F0.wireOp",EDGE,"E24")])],"isStart":true});Q41=makeQuery(id+"F11.boolean.opBoolean","SPLIT",EDGE,{"disambiguationData":[topologyDisambiguationEdgeConnected([subQ3,subQ1]),TD([makeQuery(id+"F1.opExtrude","SWEPT_FACE",FACE,{"disambiguationData":[OSD([subQ2])]})])],"derivedFrom":makeQuery(id+"F11.opExtrude","CAP_EDGE",EDGE,{"disambiguationData":[OSD([subQ0])],"isStart":true})});}
            var Q42;
            Q42=makeQuery(id+"F1.opExtrude","SWEPT_EDGE",EDGE,{"disambiguationData":[OSD([sQuery(id+"F0.wireOp",EDGE,"E12"),sQuery(id+"F0.wireOp",EDGE,"E24")])]});
            var Q43;
            {var subQ0=sQuery(id+"F0.wireOp",EDGE,"E24");var subQ1=sQuery(id+"F3.wireOp",EDGE,"E32");Q43=makeQuery(id+"F4.boolean.opBoolean","SPLIT",EDGE,{"disambiguationData":[TD([makeQuery(id+"F1.opExtrude","SWEPT_FACE",FACE,{"disambiguationData":[OSD([subQ0])]})])],"derivedFrom":makeQuery(id+"F4.opExtrude","CAP_EDGE",EDGE,{"disambiguationData":[OSD([subQ1])],"isStart":true})});}
            var Q44;
            {var subQ0=sQuery(id+"F3.wireOp",EDGE,"E32");var subQ1=sQuery(id+"F3.wireOp",EDGE,"E29");var subQ2=sQuery(id+"F0.wireOp",EDGE,"E12");Q44=makeQuery(id+"F11.boolean.opBoolean","SPLIT",EDGE,{"disambiguationData":[TD([makeQuery(id+"F1.opExtrude","SWEPT_FACE",FACE,{"disambiguationData":[OSD([subQ2])]})])],"derivedFrom":makeQuery(id+"F4.opExtrude","SWEPT_EDGE",EDGE,{"disambiguationData":[OSD([subQ1,subQ0])]})});}
            var Q45;
            Q45=makeQuery(id+"F11.boolean.opBoolean","INTERSECT",EDGE,{"derivedFrom":[makeQuery(id+"F4.opExtrude","SWEPT_FACE",FACE,{"disambiguationData":[OSD([sQuery(id+"F3.wireOp",EDGE,"E29")])]}),makeQuery(id+"F11.opExtrude","SWEPT_FACE",FACE,{"disambiguationData":[OSD([sQuery(id+"F10.wireOp",EDGE,"E53")])]})]});
            var Q46;
            Q46=makeQuery(id+"F11.boolean.opBoolean","INTERSECT",EDGE,{"derivedFrom":[makeQuery(id+"F4.opExtrude","SWEPT_FACE",FACE,{"disambiguationData":[OSD([sQuery(id+"F3.wireOp",EDGE,"E29")])]}),makeQuery(id+"F11.opExtrude","CAP_FACE",FACE,{"disambiguationData":[OSD([sQuery(id+"F10.wireOp",EDGE,"E51"),sQuery(id+"F10.wireOp",EDGE,"E52"),sQuery(id+"F10.wireOp",EDGE,"E53"),sQuery(id+"F10.wireOp",EDGE,"E56")])],"isStart":false})]});
            var Q47;
            Q47=makeQuery(id+"F11.boolean.opBoolean","INTERSECT",EDGE,{"derivedFrom":[makeQuery(id+"F4.opExtrude","SWEPT_FACE",FACE,{"disambiguationData":[OSD([sQuery(id+"F3.wireOp",EDGE,"E29")])]}),makeQuery(id+"F11.opExtrude","SWEPT_FACE",FACE,{"disambiguationData":[OSD([sQuery(id+"F10.wireOp",EDGE,"E51")])]})]});
            var Q48;
            {var subQ0=sQuery(id+"F0.wireOp",EDGE,"E10");var subQ1=sQuery(id+"F3.wireOp",EDGE,"E29");Q48=makeQuery(id+"F11.boolean.opBoolean","SPLIT",EDGE,{"disambiguationData":[TD([makeQuery(id+"F1.opExtrude","SWEPT_FACE",FACE,{"disambiguationData":[OSD([subQ0])]})])],"derivedFrom":makeQuery(id+"F4.opExtrude","SWEPT_EDGE",EDGE,{"disambiguationData":[OSD([subQ1,sQuery(id+"F3.wireOp",EDGE,"E32")])]})});}
            var Q49;
            {var subQ0=sQuery(id+"F0.wireOp",EDGE,"E24");var subQ1=sQuery(id+"F0.wireOp",EDGE,"E10");var subQ2=makeQuery(id+"F1.opExtrude","SWEPT_FACE",FACE,{"disambiguationData":[OSD([subQ1])]});Q49=makeQuery(id+"F4.boolean.opBoolean","SPLIT",EDGE,{"disambiguationData":[TD([makeQuery(id+"F1.opExtrude","SWEPT_FACE",FACE,{"disambiguationData":[OSD([subQ0])]})])],"derivedFrom":makeQuery(id+"F4.opExtrude","TWEAK_EDGE",EDGE,{"derivedFrom":[subQ2,makeQuery(id+"F3.imprint","IMPRINT",EDGE,{"derivedFrom":sQuery(id+"F3.wireOp",EDGE,"E32")})]})});}
            var Q50;
            Q50=makeQuery(id+"F1.opExtrude","SWEPT_EDGE",EDGE,{"disambiguationData":[OSD([sQuery(id+"F0.wireOp",EDGE,"E10"),sQuery(id+"F0.wireOp",EDGE,"E24")])]});
            var Q51;
            {var subQ0=sQuery(id+"F10.wireOp",EDGE,"E51");var subQ1=makeQuery(id+"F11.opExtrude","SWEPT_FACE",FACE,{"disambiguationData":[OSD([subQ0])]});var subQ2=sQuery(id+"F0.wireOp",EDGE,"E24");var subQ3=makeQuery(id+"F1.opExtrude","CAP_FACE",FACE,{"disambiguationData":[OSD([sQuery(id+"F0.wireOp",EDGE,"E0.left"),sQuery(id+"F0.wireOp",EDGE,"E0.right"),sQuery(id+"F0.wireOp",EDGE,"E2"),sQuery(id+"F0.wireOp",EDGE,"E4"),sQuery(id+"F0.wireOp",EDGE,"E6"),sQuery(id+"F0.wireOp",EDGE,"E8"),sQuery(id+"F0.wireOp",EDGE,"E10"),sQuery(id+"F0.wireOp",EDGE,"E12"),sQuery(id+"F0.wireOp",EDGE,"E14"),sQuery(id+"F0.wireOp",EDGE,"E16"),sQuery(id+"F0.wireOp",EDGE,"E19"),sQuery(id+"F0.wireOp",EDGE,"E20"),sQuery(id+"F0.wireOp",EDGE,"E21"),sQuery(id+"F0.wireOp",EDGE,"E22"),sQuery(id+"F0.wireOp",EDGE,"E23"),subQ2])],"isStart":true});Q51=makeQuery(id+"F11.boolean.opBoolean","SPLIT",EDGE,{"disambiguationData":[topologyDisambiguationEdgeConnected([subQ3,subQ1]),TD([makeQuery(id+"F1.opExtrude","SWEPT_FACE",FACE,{"disambiguationData":[OSD([subQ2])]})])],"derivedFrom":makeQuery(id+"F11.opExtrude","CAP_EDGE",EDGE,{"disambiguationData":[OSD([subQ0])],"isStart":true})});}
            var Q52;
            {var subQ1=sQuery(id+"F10.wireOp",EDGE,"E53");var subQ2=sQuery(id+"F0.wireOp",EDGE,"E24");var subQ3=makeQuery(id+"F11.opExtrude","SWEPT_FACE",FACE,{"disambiguationData":[OSD([subQ1])]});var subQ4=makeQuery(id+"F1.opExtrude","CAP_FACE",FACE,{"disambiguationData":[OSD([sQuery(id+"F0.wireOp",EDGE,"E0.left"),sQuery(id+"F0.wireOp",EDGE,"E0.right"),sQuery(id+"F0.wireOp",EDGE,"E2"),sQuery(id+"F0.wireOp",EDGE,"E4"),sQuery(id+"F0.wireOp",EDGE,"E6"),sQuery(id+"F0.wireOp",EDGE,"E8"),sQuery(id+"F0.wireOp",EDGE,"E10"),sQuery(id+"F0.wireOp",EDGE,"E12"),sQuery(id+"F0.wireOp",EDGE,"E14"),sQuery(id+"F0.wireOp",EDGE,"E16"),sQuery(id+"F0.wireOp",EDGE,"E19"),sQuery(id+"F0.wireOp",EDGE,"E20"),sQuery(id+"F0.wireOp",EDGE,"E21"),sQuery(id+"F0.wireOp",EDGE,"E22"),sQuery(id+"F0.wireOp",EDGE,"E23"),subQ2])],"isStart":true});Q52=makeQuery(id+"F11.boolean.opBoolean","SPLIT",EDGE,{"disambiguationData":[topologyDisambiguationEdgeConnected([subQ4,subQ3]),TD([makeQuery(id+"F1.opExtrude","SWEPT_FACE",FACE,{"disambiguationData":[OSD([subQ2])]})])],"derivedFrom":makeQuery(id+"F11.opExtrude","CAP_EDGE",EDGE,{"disambiguationData":[OSD([subQ1])],"isStart":true})});}
            var Q53;
            Q53=makeQuery(id+"F1.opExtrude","SWEPT_EDGE",EDGE,{"disambiguationData":[OSD([sQuery(id+"F0.wireOp",EDGE,"E16"),sQuery(id+"F0.wireOp",EDGE,"E23")])]});
            var Q54;
            {var subQ1=sQuery(id+"F0.wireOp",EDGE,"E23");var subQ2=sQuery(id+"F0.wireOp",EDGE,"E4");Q54=makeQuery(id+"F7.boolean.opBoolean","SPLIT",EDGE,{"disambiguationData":[TD([makeQuery(id+"F1.opExtrude","SWEPT_FACE",FACE,{"disambiguationData":[OSD([subQ1])]})])],"derivedFrom":makeQuery(id+"F7.opExtrude","TWEAK_EDGE",EDGE,{"derivedFrom":[makeQuery(id+"F1.opExtrude","SWEPT_FACE",FACE,{"disambiguationData":[OSD([subQ2])]}),makeQuery(id+"F6.imprint","IMPRINT",EDGE,{"derivedFrom":sQuery(id+"F6.wireOp",EDGE,"E44.MirrorCS")})]})});}
            var Q55;
            {var subQ1=sQuery(id+"F6.wireOp",EDGE,"E45.MirrorCS");var subQ2=sQuery(id+"F0.wireOp",EDGE,"E16");Q55=makeQuery(id+"F11.boolean.opBoolean","SPLIT",EDGE,{"disambiguationData":[TD([makeQuery(id+"F1.opExtrude","SWEPT_FACE",FACE,{"disambiguationData":[OSD([subQ2])]})])],"derivedFrom":makeQuery(id+"F7.opExtrude","SWEPT_EDGE",EDGE,{"disambiguationData":[OSD([sQuery(id+"F6.wireOp",EDGE,"E44.MirrorCS"),subQ1])]})});}
            var Q56;
            Q56=makeQuery(id+"F11.boolean.opBoolean","INTERSECT",EDGE,{"derivedFrom":[makeQuery(id+"F7.opExtrude","SWEPT_FACE",FACE,{"disambiguationData":[OSD([sQuery(id+"F6.wireOp",EDGE,"E45.MirrorCS")])]}),makeQuery(id+"F11.opExtrude","SWEPT_FACE",FACE,{"disambiguationData":[OSD([sQuery(id+"F10.wireOp",EDGE,"E57.3.0")])]})]});
            var Q57;
            Q57=makeQuery(id+"F11.boolean.opBoolean","INTERSECT",EDGE,{"derivedFrom":[makeQuery(id+"F7.opExtrude","SWEPT_FACE",FACE,{"disambiguationData":[OSD([sQuery(id+"F6.wireOp",EDGE,"E45.MirrorCS")])]}),makeQuery(id+"F11.opExtrude","CAP_FACE",FACE,{"disambiguationData":[OSD([sQuery(id+"F10.wireOp",EDGE,"E57.3.0"),sQuery(id+"F10.wireOp",EDGE,"E57.3.1"),sQuery(id+"F10.wireOp",EDGE,"E57.3.2"),sQuery(id+"F10.wireOp",EDGE,"E57.3.3")])],"isStart":false})]});
            var Q58;
            Q58=makeQuery(id+"F11.boolean.opBoolean","INTERSECT",EDGE,{"derivedFrom":[makeQuery(id+"F7.opExtrude","SWEPT_FACE",FACE,{"disambiguationData":[OSD([sQuery(id+"F6.wireOp",EDGE,"E45.MirrorCS")])]}),makeQuery(id+"F11.opExtrude","SWEPT_FACE",FACE,{"disambiguationData":[OSD([sQuery(id+"F10.wireOp",EDGE,"E57.3.2")])]})]});
            var Q59;
            {var subQ0=sQuery(id+"F6.wireOp",EDGE,"E45.MirrorCS");var subQ1=sQuery(id+"F6.wireOp",EDGE,"E44.MirrorCS");var subQ2=sQuery(id+"F0.wireOp",EDGE,"E14");Q59=makeQuery(id+"F11.boolean.opBoolean","SPLIT",EDGE,{"disambiguationData":[TD([makeQuery(id+"F1.opExtrude","SWEPT_FACE",FACE,{"disambiguationData":[OSD([subQ2])]})])],"derivedFrom":makeQuery(id+"F7.opExtrude","SWEPT_EDGE",EDGE,{"disambiguationData":[OSD([subQ1,subQ0])]})});}
            var Q60;
            {var subQ1=sQuery(id+"F6.wireOp",EDGE,"E44.MirrorCS");var subQ3=sQuery(id+"F0.wireOp",EDGE,"E23");Q60=makeQuery(id+"F7.boolean.opBoolean","SPLIT",EDGE,{"disambiguationData":[TD([makeQuery(id+"F1.opExtrude","SWEPT_FACE",FACE,{"disambiguationData":[OSD([subQ3])]})])],"derivedFrom":makeQuery(id+"F7.opExtrude","CAP_EDGE",EDGE,{"disambiguationData":[OSD([subQ1])],"isStart":true})});}
            var Q61;
            Q61=makeQuery(id+"F1.opExtrude","SWEPT_EDGE",EDGE,{"disambiguationData":[OSD([sQuery(id+"F0.wireOp",EDGE,"E14"),sQuery(id+"F0.wireOp",EDGE,"E23")])]});
            var Q62;
            {var subQ0=sQuery(id+"F10.wireOp",EDGE,"E57.3.2");var subQ2=sQuery(id+"F0.wireOp",EDGE,"E23");var subQ3=makeQuery(id+"F1.opExtrude","CAP_FACE",FACE,{"disambiguationData":[OSD([sQuery(id+"F0.wireOp",EDGE,"E0.left"),sQuery(id+"F0.wireOp",EDGE,"E0.right"),sQuery(id+"F0.wireOp",EDGE,"E2"),sQuery(id+"F0.wireOp",EDGE,"E4"),sQuery(id+"F0.wireOp",EDGE,"E6"),sQuery(id+"F0.wireOp",EDGE,"E8"),sQuery(id+"F0.wireOp",EDGE,"E10"),sQuery(id+"F0.wireOp",EDGE,"E12"),sQuery(id+"F0.wireOp",EDGE,"E14"),sQuery(id+"F0.wireOp",EDGE,"E16"),sQuery(id+"F0.wireOp",EDGE,"E19"),sQuery(id+"F0.wireOp",EDGE,"E20"),sQuery(id+"F0.wireOp",EDGE,"E21"),sQuery(id+"F0.wireOp",EDGE,"E22"),subQ2,sQuery(id+"F0.wireOp",EDGE,"E24")])],"isStart":true});var subQ4=makeQuery(id+"F11.opExtrude","SWEPT_FACE",FACE,{"disambiguationData":[OSD([subQ0])]});Q62=makeQuery(id+"F11.boolean.opBoolean","SPLIT",EDGE,{"disambiguationData":[topologyDisambiguationEdgeConnected([subQ3,subQ4]),TD([makeQuery(id+"F1.opExtrude","SWEPT_FACE",FACE,{"disambiguationData":[OSD([subQ2])]})])],"derivedFrom":makeQuery(id+"F11.opExtrude","CAP_EDGE",EDGE,{"disambiguationData":[OSD([subQ0])],"isStart":true})});}
            var Q63;
            {var subQ0=sQuery(id+"F10.wireOp",EDGE,"E57.3.0");var subQ1=makeQuery(id+"F11.opExtrude","SWEPT_FACE",FACE,{"disambiguationData":[OSD([subQ0])]});var subQ2=sQuery(id+"F0.wireOp",EDGE,"E23");var subQ3=makeQuery(id+"F1.opExtrude","CAP_FACE",FACE,{"disambiguationData":[OSD([sQuery(id+"F0.wireOp",EDGE,"E0.left"),sQuery(id+"F0.wireOp",EDGE,"E0.right"),sQuery(id+"F0.wireOp",EDGE,"E2"),sQuery(id+"F0.wireOp",EDGE,"E4"),sQuery(id+"F0.wireOp",EDGE,"E6"),sQuery(id+"F0.wireOp",EDGE,"E8"),sQuery(id+"F0.wireOp",EDGE,"E10"),sQuery(id+"F0.wireOp",EDGE,"E12"),sQuery(id+"F0.wireOp",EDGE,"E14"),sQuery(id+"F0.wireOp",EDGE,"E16"),sQuery(id+"F0.wireOp",EDGE,"E19"),sQuery(id+"F0.wireOp",EDGE,"E20"),sQuery(id+"F0.wireOp",EDGE,"E21"),sQuery(id+"F0.wireOp",EDGE,"E22"),subQ2,sQuery(id+"F0.wireOp",EDGE,"E24")])],"isStart":true});Q63=makeQuery(id+"F11.boolean.opBoolean","SPLIT",EDGE,{"disambiguationData":[topologyDisambiguationEdgeConnected([subQ3,subQ1]),TD([makeQuery(id+"F1.opExtrude","SWEPT_FACE",FACE,{"disambiguationData":[OSD([subQ2])]})])],"derivedFrom":makeQuery(id+"F11.opExtrude","CAP_EDGE",EDGE,{"disambiguationData":[OSD([subQ0])],"isStart":true})});}
            fillet(context, id + "F12", {"entities" : qUnion([Q0, Q1, Q2, Q3, Q4, Q5, Q6, Q7, Q8, Q9, Q10, Q11, Q12, Q13, Q14, Q15, Q16, Q17, Q18, Q19, Q20, Q21, Q22, Q23, Q24, Q25, Q26, Q27, Q28, Q29, Q30, Q31, Q32, Q33, Q34, Q35, Q36, Q37, Q38, Q39, Q40, Q41, Q42, Q43, Q44, Q45, Q46, Q47, Q48, Q49, Q50, Q51, Q52, Q53, Q54, Q55, Q56, Q57, Q58, Q59, Q60, Q61, Q62, Q63]), "radius" : 1 * mm, "tangentPropagation" : true, "allowEdgeOverflow" : false});
        }
        {
            var Q0;
            Q0=makeQuery(id+"F4.opExtrude","SWEPT_EDGE",EDGE,{"disambiguationData":[OSD([sQuery(id+"F3.wireOp",EDGE,"E30"),sQuery(id+"F3.wireOp",EDGE,"E31")])]});
            var Q1;
            Q1=makeQuery(id+"F7.opExtrude","SWEPT_EDGE",EDGE,{"disambiguationData":[OSD([sQuery(id+"F6.wireOp",EDGE,"E41"),sQuery(id+"F6.wireOp",EDGE,"E42")])]});
            var Q2;
            Q2=makeQuery(id+"F4.opExtrude","SWEPT_EDGE",EDGE,{"disambiguationData":[OSD([sQuery(id+"F3.wireOp",EDGE,"E34.MirrorCS"),sQuery(id+"F3.wireOp",EDGE,"E37.MirrorCS")])]});
            var Q3;
            Q3=makeQuery(id+"F4.opExtrude","SWEPT_EDGE",EDGE,{"disambiguationData":[OSD([sQuery(id+"F3.wireOp",EDGE,"E29"),sQuery(id+"F3.wireOp",EDGE,"E30")])]});
            var Q4;
            Q4=makeQuery(id+"F7.opExtrude","SWEPT_EDGE",EDGE,{"disambiguationData":[OSD([sQuery(id+"F6.wireOp",EDGE,"E40"),sQuery(id+"F6.wireOp",EDGE,"E41")])]});
            var Q5;
            Q5=makeQuery(id+"F4.opExtrude","SWEPT_EDGE",EDGE,{"disambiguationData":[OSD([sQuery(id+"F3.wireOp",EDGE,"E36.MirrorCS"),sQuery(id+"F3.wireOp",EDGE,"E37.MirrorCS")])]});
            var Q6;
            Q6=makeQuery(id+"F7.opExtrude","SWEPT_EDGE",EDGE,{"disambiguationData":[OSD([sQuery(id+"F6.wireOp",EDGE,"E43.MirrorCS"),sQuery(id+"F6.wireOp",EDGE,"E46.MirrorCS")])]});
            var Q7;
            Q7=makeQuery(id+"F7.opExtrude","SWEPT_EDGE",EDGE,{"disambiguationData":[OSD([sQuery(id+"F6.wireOp",EDGE,"E45.MirrorCS"),sQuery(id+"F6.wireOp",EDGE,"E46.MirrorCS")])]});
            fillet(context, id + "F13", {"entities" : qUnion([Q0, Q1, Q2, Q3, Q4, Q5, Q6, Q7]), "radius" : 2 * mm, "tangentPropagation" : true, "allowEdgeOverflow" : false});
        }
        {
            var Q0;
            Q0=makeQuery(id+"F7.opExtrude","TWEAK_EDGE",EDGE,{"derivedFrom":[makeQuery(id+"F1.opExtrude","SWEPT_FACE",FACE,{"disambiguationData":[OSD([sQuery(id+"F0.wireOp",EDGE,"E4")])]}),makeQuery(id+"F6.imprint","IMPRINT",EDGE,{"derivedFrom":sQuery(id+"F6.wireOp",EDGE,"E40")})]});
            var Q1;
            Q1=makeQuery(id+"F7.opExtrude","CAP_EDGE",EDGE,{"disambiguationData":[OSD([sQuery(id+"F6.wireOp",EDGE,"E41")])],"isStart":true});
            var Q2;
            Q2=makeQuery(id+"F4.opExtrude","TWEAK_EDGE",EDGE,{"derivedFrom":[makeQuery(id+"F1.opExtrude","SWEPT_FACE",FACE,{"disambiguationData":[OSD([sQuery(id+"F0.wireOp",EDGE,"E10")])]}),makeQuery(id+"F3.imprint","IMPRINT",EDGE,{"derivedFrom":sQuery(id+"F3.wireOp",EDGE,"E29")})]});
            var Q3;
            Q3=makeQuery(id+"F7.opExtrude","CAP_EDGE",EDGE,{"disambiguationData":[OSD([sQuery(id+"F6.wireOp",EDGE,"E46.MirrorCS")])],"isStart":true});
            var Q4;
            Q4=makeQuery(id+"F4.opExtrude","CAP_EDGE",EDGE,{"disambiguationData":[OSD([sQuery(id+"F3.wireOp",EDGE,"E29")])],"isStart":true});
            var Q5;
            Q5=makeQuery(id+"F7.opExtrude","TWEAK_EDGE",EDGE,{"derivedFrom":[makeQuery(id+"F1.opExtrude","SWEPT_FACE",FACE,{"disambiguationData":[OSD([sQuery(id+"F0.wireOp",EDGE,"E4")])]}),makeQuery(id+"F6.imprint","IMPRINT",EDGE,{"derivedFrom":sQuery(id+"F6.wireOp",EDGE,"E46.MirrorCS")})]});
            var Q6;
            Q6=makeQuery(id+"F4.opExtrude","CAP_EDGE",EDGE,{"disambiguationData":[OSD([sQuery(id+"F3.wireOp",EDGE,"E37.MirrorCS")])],"isStart":true});
            var Q7;
            Q7=makeQuery(id+"F4.opExtrude","TWEAK_EDGE",EDGE,{"derivedFrom":[makeQuery(id+"F1.opExtrude","SWEPT_FACE",FACE,{"disambiguationData":[OSD([sQuery(id+"F0.wireOp",EDGE,"E10")])]}),makeQuery(id+"F3.imprint","IMPRINT",EDGE,{"derivedFrom":sQuery(id+"F3.wireOp",EDGE,"E37.MirrorCS")})]});
            var Q8;
            Q8=makeQuery(id+"F1.opExtrude","CAP_EDGE",EDGE,{"disambiguationData":[OSD([sQuery(id+"F0.wireOp",EDGE,"E20")])],"isStart":true});
            var Q9;
            Q9=makeQuery(id+"F1.opExtrude","CAP_EDGE",EDGE,{"disambiguationData":[OSD([sQuery(id+"F0.wireOp",EDGE,"E0.left")])],"isStart":true});
            var Q10;
            Q10=makeQuery(id+"F1.opExtrude","CAP_EDGE",EDGE,{"disambiguationData":[OSD([sQuery(id+"F0.wireOp",EDGE,"E19")])],"isStart":true});
            var Q11;
            Q11=makeQuery(id+"F1.opExtrude","CAP_EDGE",EDGE,{"disambiguationData":[OSD([sQuery(id+"F0.wireOp",EDGE,"E0.right")])],"isStart":true});
            fillet(context, id + "F14", {"entities" : qUnion([Q0, Q1, Q2, Q3, Q4, Q5, Q6, Q7, Q8, Q9, Q10, Q11]), "radius" : 1 * mm, "tangentPropagation" : true, "allowEdgeOverflow" : false});
        }
        {
            var Q0;
            Q0=makeQuery(id+"F1.opExtrude","CAP_EDGE",EDGE,{"disambiguationData":[OSD([sQuery(id+"F0.wireOp",EDGE,"E22")])],"isStart":false});
            var Q1;
            Q1=makeQuery(id+"F11.opExtrude","CAP_EDGE",EDGE,{"disambiguationData":[OSD([sQuery(id+"F10.wireOp",EDGE,"E57.3.2")])],"isStart":false});
            var Q2;
            Q2=makeQuery(id+"F11.opExtrude","CAP_EDGE",EDGE,{"disambiguationData":[OSD([sQuery(id+"F10.wireOp",EDGE,"E57.3.1")])],"isStart":false});
            var Q3;
            Q3=makeQuery(id+"F11.opExtrude","CAP_EDGE",EDGE,{"disambiguationData":[OSD([sQuery(id+"F10.wireOp",EDGE,"E57.3.0")])],"isStart":false});
            var Q4;
            Q4=makeQuery(id+"F11.opExtrude","CAP_EDGE",EDGE,{"disambiguationData":[OSD([sQuery(id+"F10.wireOp",EDGE,"E57.2.2")])],"isStart":false});
            var Q5;
            Q5=makeQuery(id+"F11.opExtrude","CAP_EDGE",EDGE,{"disambiguationData":[OSD([sQuery(id+"F10.wireOp",EDGE,"E57.2.1")])],"isStart":false});
            var Q6;
            Q6=makeQuery(id+"F11.opExtrude","CAP_EDGE",EDGE,{"disambiguationData":[OSD([sQuery(id+"F10.wireOp",EDGE,"E57.2.0")])],"isStart":false});
            var Q7;
            {var subQ1=sQuery(id+"F0.wireOp",EDGE,"E22");var subQ2=sQuery(id+"F0.wireOp",EDGE,"E6");Q7=makeQuery(id+"F11.boolean.opBoolean","SPLIT",EDGE,{"disambiguationData":[TD([makeQuery(id+"F1.opExtrude","SWEPT_FACE",FACE,{"disambiguationData":[OSD([subQ2])]})])],"derivedFrom":makeQuery(id+"F1.opExtrude","CAP_EDGE",EDGE,{"disambiguationData":[OSD([subQ1])],"isStart":true})});}
            var Q8;
            {var subQ0=sQuery(id+"F0.wireOp",EDGE,"E22");var subQ1=sQuery(id+"F0.wireOp",EDGE,"E8");Q8=makeQuery(id+"F11.boolean.opBoolean","SPLIT",EDGE,{"disambiguationData":[TD([makeQuery(id+"F1.opExtrude","SWEPT_FACE",FACE,{"disambiguationData":[OSD([subQ1])]})])],"derivedFrom":makeQuery(id+"F1.opExtrude","CAP_EDGE",EDGE,{"disambiguationData":[OSD([subQ0])],"isStart":true})});}
            var Q9;
            {var subQ1=sQuery(id+"F0.wireOp",EDGE,"E23");var subQ2=sQuery(id+"F0.wireOp",EDGE,"E16");Q9=makeQuery(id+"F11.boolean.opBoolean","SPLIT",EDGE,{"disambiguationData":[TD([makeQuery(id+"F1.opExtrude","SWEPT_FACE",FACE,{"disambiguationData":[OSD([subQ2])]})])],"derivedFrom":makeQuery(id+"F1.opExtrude","CAP_EDGE",EDGE,{"disambiguationData":[OSD([subQ1])],"isStart":true})});}
            var Q10;
            {var subQ0=sQuery(id+"F0.wireOp",EDGE,"E14");var subQ1=sQuery(id+"F0.wireOp",EDGE,"E23");Q10=makeQuery(id+"F11.boolean.opBoolean","SPLIT",EDGE,{"disambiguationData":[TD([makeQuery(id+"F1.opExtrude","SWEPT_FACE",FACE,{"disambiguationData":[OSD([subQ0])]})])],"derivedFrom":makeQuery(id+"F1.opExtrude","CAP_EDGE",EDGE,{"disambiguationData":[OSD([subQ1])],"isStart":true})});}
            var Q11;
            Q11=makeQuery(id+"F11.opExtrude","CAP_EDGE",EDGE,{"disambiguationData":[OSD([sQuery(id+"F10.wireOp",EDGE,"E51")])],"isStart":false});
            var Q12;
            Q12=makeQuery(id+"F11.opExtrude","CAP_EDGE",EDGE,{"disambiguationData":[OSD([sQuery(id+"F10.wireOp",EDGE,"E56")])],"isStart":false});
            var Q13;
            Q13=makeQuery(id+"F11.opExtrude","CAP_EDGE",EDGE,{"disambiguationData":[OSD([sQuery(id+"F10.wireOp",EDGE,"E53")])],"isStart":false});
            var Q14;
            {var subQ0=sQuery(id+"F0.wireOp",EDGE,"E24");var subQ1=sQuery(id+"F0.wireOp",EDGE,"E12");Q14=makeQuery(id+"F11.boolean.opBoolean","SPLIT",EDGE,{"disambiguationData":[TD([makeQuery(id+"F1.opExtrude","SWEPT_FACE",FACE,{"disambiguationData":[OSD([subQ1])]})])],"derivedFrom":makeQuery(id+"F1.opExtrude","CAP_EDGE",EDGE,{"disambiguationData":[OSD([subQ0])],"isStart":true})});}
            var Q15;
            {var subQ0=sQuery(id+"F0.wireOp",EDGE,"E10");var subQ1=sQuery(id+"F0.wireOp",EDGE,"E24");Q15=makeQuery(id+"F11.boolean.opBoolean","SPLIT",EDGE,{"disambiguationData":[TD([makeQuery(id+"F1.opExtrude","SWEPT_FACE",FACE,{"disambiguationData":[OSD([subQ0])]})])],"derivedFrom":makeQuery(id+"F1.opExtrude","CAP_EDGE",EDGE,{"disambiguationData":[OSD([subQ1])],"isStart":true})});}
            var Q16;
            Q16=makeQuery(id+"F11.opExtrude","CAP_EDGE",EDGE,{"disambiguationData":[OSD([sQuery(id+"F10.wireOp",EDGE,"E57.1.2")])],"isStart":false});
            var Q17;
            Q17=makeQuery(id+"F11.opExtrude","CAP_EDGE",EDGE,{"disambiguationData":[OSD([sQuery(id+"F10.wireOp",EDGE,"E57.1.1")])],"isStart":false});
            var Q18;
            Q18=makeQuery(id+"F11.opExtrude","CAP_EDGE",EDGE,{"disambiguationData":[OSD([sQuery(id+"F10.wireOp",EDGE,"E57.1.0")])],"isStart":false});
            var Q19;
            {var subQ0=sQuery(id+"F0.wireOp",EDGE,"E2");var subQ1=sQuery(id+"F0.wireOp",EDGE,"E21");Q19=makeQuery(id+"F11.boolean.opBoolean","SPLIT",EDGE,{"disambiguationData":[TD([makeQuery(id+"F1.opExtrude","SWEPT_FACE",FACE,{"disambiguationData":[OSD([subQ0])]})])],"derivedFrom":makeQuery(id+"F1.opExtrude","CAP_EDGE",EDGE,{"disambiguationData":[OSD([subQ1])],"isStart":true})});}
            var Q20;
            {var subQ0=sQuery(id+"F0.wireOp",EDGE,"E4");var subQ1=sQuery(id+"F0.wireOp",EDGE,"E21");Q20=makeQuery(id+"F11.boolean.opBoolean","SPLIT",EDGE,{"disambiguationData":[TD([makeQuery(id+"F1.opExtrude","SWEPT_FACE",FACE,{"disambiguationData":[OSD([subQ0])]})])],"derivedFrom":makeQuery(id+"F1.opExtrude","CAP_EDGE",EDGE,{"disambiguationData":[OSD([subQ1])],"isStart":true})});}
            fillet(context, id + "F15", {"entities" : qUnion([Q0, Q1, Q2, Q3, Q4, Q5, Q6, Q7, Q8, Q9, Q10, Q11, Q12, Q13, Q14, Q15, Q16, Q17, Q18, Q19, Q20]), "radius" : 0.5 * mm, "tangentPropagation" : true, "allowEdgeOverflow" : false});
        }
    });
